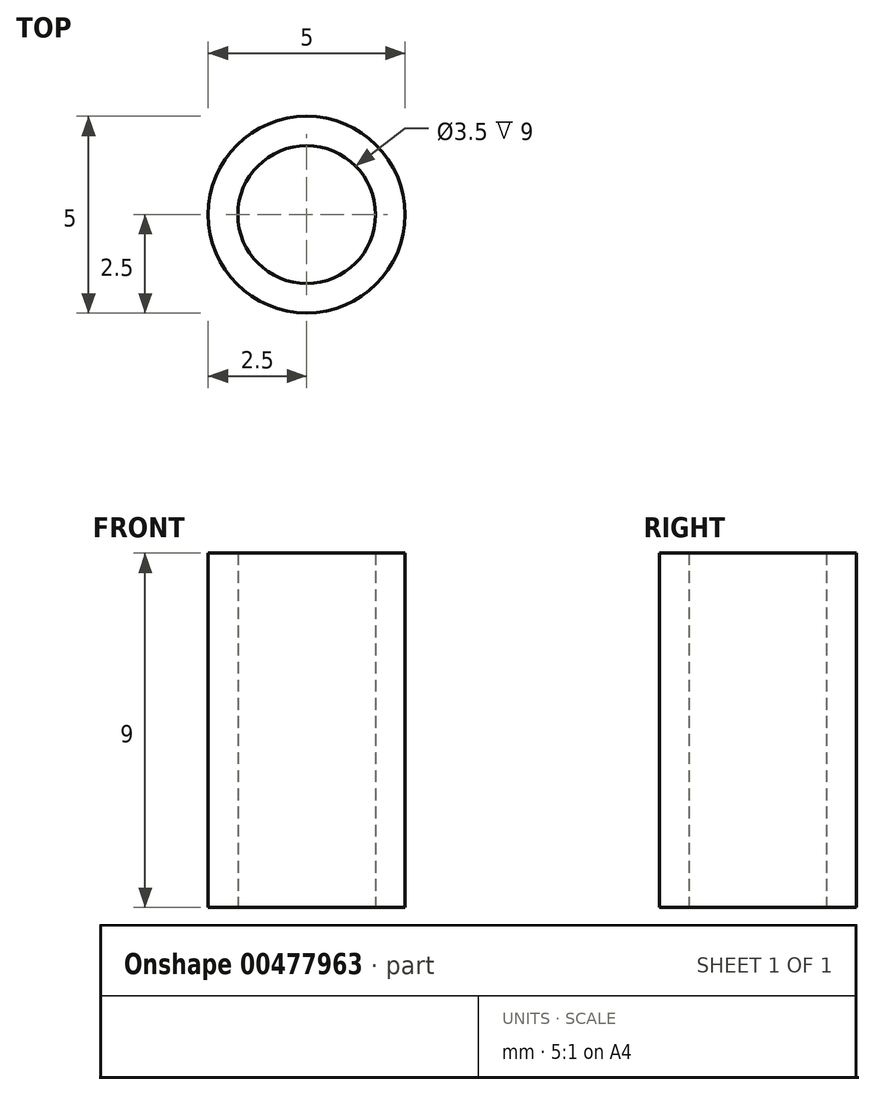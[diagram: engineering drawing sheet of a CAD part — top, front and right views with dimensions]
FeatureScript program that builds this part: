
annotation { "Feature Type Name" : "Feature", "Feature Type Description" : "" }
export const myFeature = defineFeature(function(context is Context, id is Id, definition is map)
    precondition{}
    {
        {
            var Q0;
            Q0=qCreatedBy(makeId("Top.planeOp"),FACE);
            var sketch = newSketch(context, id + "F0", { "sketchPlane" : qUnion([Q0])});
            skCircle(sketch, "E0", {"center": v(0, 0) * mm, "radius": 1.75 * mm});
            skCircle(sketch, "E1", {"center": v(0, 0) * mm, "radius": 2.5 * mm});
            skSolve(sketch);
        }
        {
            var Q0;
            Q0 = qSketchRegion(id + "F0", true);
            extrude(context, id + "F1", {"entities" : qUnion([Q0]), "depth" : 9 * mm});
        }
    });
